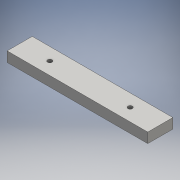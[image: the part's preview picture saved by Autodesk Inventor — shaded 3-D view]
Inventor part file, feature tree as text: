
AUTODESK INVENTOR PART (.ipt)
format: ipt  version: 2016 (Build 200138000, 138)  size: 97,792 bytes
history: native  units: mm
features: sketch x2, extrude x1, hole x1
ambient origin geometry x8: Origin, YZ Plane, XZ Plane, XY Plane, X Axis, Y Axis, Z Axis, Center Point
bodies: Solid1 (feature_tree)
feature tree (4):
  extrude  "Extrusion1"  Depth=25.0mm
  hole  "Hole1"  [1 undecoded]
  sketch  "Sketch1"  dims[d0=140.0mm d1=25.0mm]
  sketch  "Sketch2"  dims[d2=70.0mm d3=12.5mm d4=10.0mm d5=0.0mm d6=80.0mm d7=40.0mm d8=4.5mm d9=6.0mm d10=4.0mm d11=2.0mm d12=90.0deg d13=8.0mm d14=20.594885mm]
note: 1 required parameter value undecoded (feature->parameter linkage not recoverable at this tier; creation-order binding heuristic only, values carry confidence <= 0.55)
